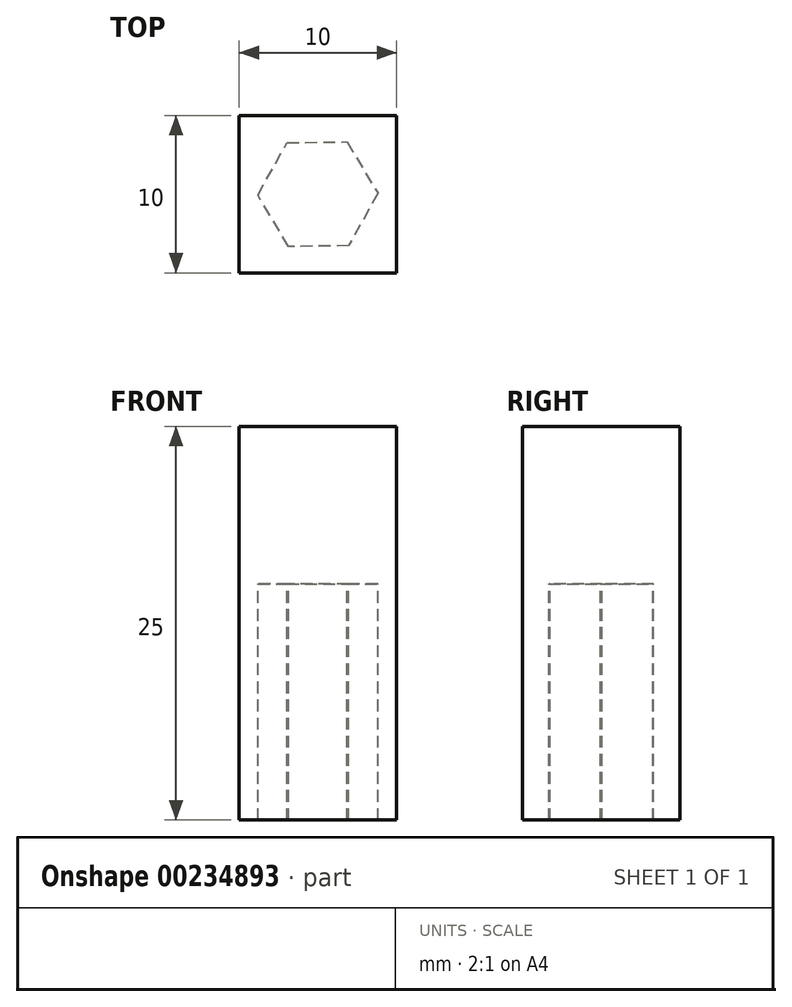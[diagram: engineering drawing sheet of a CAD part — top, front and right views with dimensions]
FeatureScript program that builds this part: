
annotation { "Feature Type Name" : "Feature", "Feature Type Description" : "" }
export const myFeature = defineFeature(function(context is Context, id is Id, definition is map)
    precondition{}
    {
        {
            var Q0;
            Q0=qCreatedBy(makeId("Top.planeOp"),FACE);
            var sketch = newSketch(context, id + "F0", { "sketchPlane" : qUnion([Q0])});
            skCircle(sketch, "E0.cCircle", {"center": v(0, 0) * mm, "radius": 3.3 * mm, "construction": true});
            skLineSegment(sketch, "E0.0", {"start": v(1.85, 3.33) * mm, "end": v(3.81, 0.06) * mm});
            skLineSegment(sketch, "E0.1", {"start": v(3.81, 0.06) * mm, "end": v(1.96, -3.27) * mm});
            skLineSegment(sketch, "E0.2", {"start": v(1.96, -3.27) * mm, "end": v(-1.85, -3.33) * mm});
            skLineSegment(sketch, "E0.3", {"start": v(-1.85, -3.33) * mm, "end": v(-3.81, -0.06) * mm});
            skLineSegment(sketch, "E0.4", {"start": v(-3.81, -0.06) * mm, "end": v(-1.96, 3.27) * mm});
            skLineSegment(sketch, "E0.5", {"start": v(-1.96, 3.27) * mm, "end": v(1.85, 3.33) * mm});
            skPoint(sketch, "E0.0.midPoint", {"position": v(2.83, 1.7) * mm});
            skLineSegment(sketch, "E1", {"start": v(0, 0) * mm, "end": v(0, 1.19) * mm});
            skLineSegment(sketch, "E2", {"start": v(0, 0) * mm, "end": v(-5, 0) * mm});
            skLineSegment(sketch, "E3", {"start": v(-5, 0) * mm, "end": v(-5, 5) * mm});
            skLineSegment(sketch, "E4", {"start": v(-5, 5) * mm, "end": v(0, 5) * mm});
            skLineSegment(sketch, "E5.MirrorCS", {"start": v(-5, -5) * mm, "end": v(0, -5) * mm});
            skLineSegment(sketch, "E6.MirrorCS", {"start": v(-5, 0) * mm, "end": v(-5, -5) * mm});
            skLineSegment(sketch, "E7.MirrorCS", {"start": v(5, 5) * mm, "end": v(0, 5) * mm});
            skLineSegment(sketch, "E8.MirrorCS", {"start": v(5, 0) * mm, "end": v(5, 5) * mm});
            skLineSegment(sketch, "E9.MirrorCS", {"start": v(5, 0) * mm, "end": v(5, -5) * mm});
            skLineSegment(sketch, "E10.MirrorCS", {"start": v(5, -5) * mm, "end": v(0, -5) * mm});
            skSolve(sketch);
        }
        {
            var Q0;
            Q0=makeQuery(id+"F0.imprint","IMPRINT",FACE,{"disambiguationData":[TD([[makeQuery(id+"F0.imprint","IMPRINT",EDGE,{"derivedFrom":sQuery(id+"F0.wireOp",EDGE,"E0.0")}),1.0]])]});
            var Q1;
            Q1=makeQuery(id+"F0.imprint","IMPRINT",FACE,{"disambiguationData":[TD([[makeQuery(id+"F0.imprint","IMPRINT",EDGE,{"derivedFrom":sQuery(id+"F0.wireOp",EDGE,"E0.0")}),-1.0]])]});
            extrude(context, id + "F1", {"entities" : qUnion([Q0, Q1]), "depth" : 10 * mm});
        }
        {
            var Q0;
            Q0=makeQuery(id+"F0.imprint","IMPRINT",FACE,{"disambiguationData":[TD([[makeQuery(id+"F0.imprint","IMPRINT",EDGE,{"derivedFrom":sQuery(id+"F0.wireOp",EDGE,"E0.0")}),1.0]])]});
            extrude(context, id + "F2", {"entities" : qUnion([Q0]), "operationType" : NewBodyOperationType.ADD, "oppositeDirection" : true, "depth" : 15 * mm});
        }
    });
